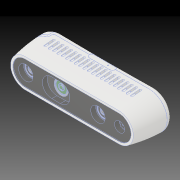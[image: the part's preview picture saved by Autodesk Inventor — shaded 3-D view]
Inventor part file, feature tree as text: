
AUTODESK INVENTOR PART (.ipt)
format: ipt  version: 2020 (Build 240168000, 168)  size: 1,148,416 bytes
history: imported  units: mm
features: other x9, projected_geometry x5, sketch x2, imported_body x1
ambient origin geometry x8: Origin, YZ Plane, XZ Plane, XY Plane, X Axis, Y Axis, Z Axis, Center Point
bodies: Solid1 (imported_parasolid), Solid2 (imported_parasolid), Solid3 (imported_parasolid), Solid4 (imported_parasolid), Solid5 (imported_parasolid), Solid6 (imported_parasolid), Solid7 (imported_parasolid), Solid8 (imported_parasolid)
feature tree (17):
  sketch  "Sketch1"
  other  "РабПлоскость1"
  sketch  "Эскиз2"
  projected_geometry  "Projected Loop1"
  projected_geometry  "Projected Loop2"
  projected_geometry  "Projected Loop3"
  projected_geometry  "Спроецированная петля4"
  projected_geometry  "Спроецированная петля5"
  other  "Cut-Extrude-Thin2[2]"
  other  "LPattern6[1]"
  other  "LPattern6[2]"
  other  "LPattern6[3]"
  other  "LPattern6[4]"
  other  "LPattern6[5]"
  other  "Dome2"
  other  "Boss-Extrude6"
  imported_body  NMx_Import_Brep_tag  [imported B-rep: ~17 faces, bbox_mm=None]
